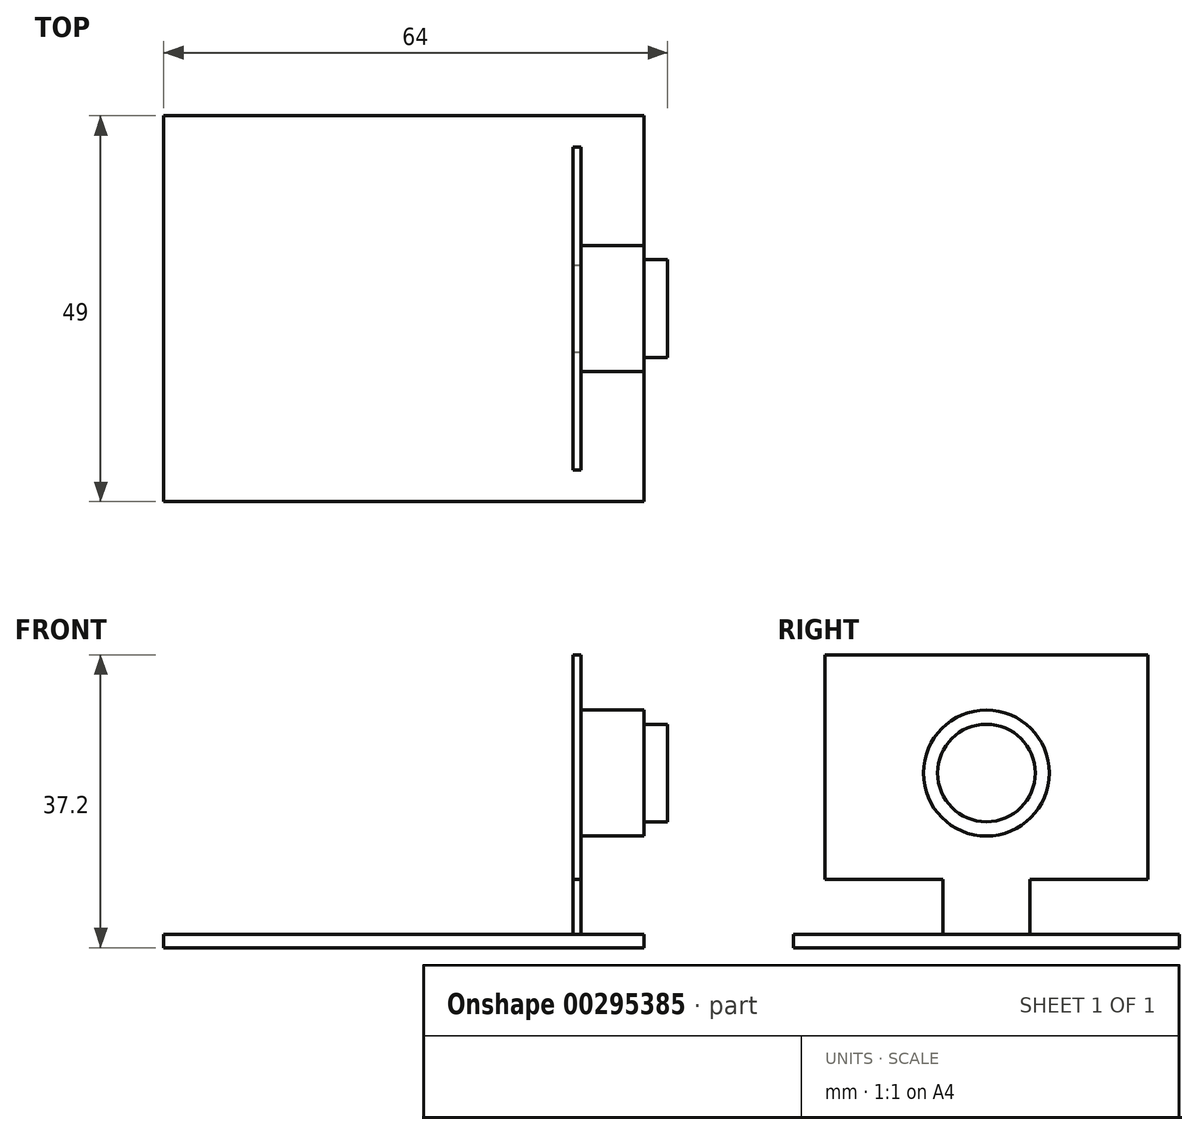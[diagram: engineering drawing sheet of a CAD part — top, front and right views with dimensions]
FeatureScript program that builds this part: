
annotation { "Feature Type Name" : "Feature", "Feature Type Description" : "" }
export const myFeature = defineFeature(function(context is Context, id is Id, definition is map)
    precondition{}
    {
        {
            var Q0;
            Q0=qCreatedBy(makeId("Top.planeOp"),FACE);
            var sketch = newSketch(context, id + "F0", { "sketchPlane" : qUnion([Q0])});
            skLineSegment(sketch, "E0.bottom", {"start": v(0, 0) * mm, "end": v(-61, 0) * mm});
            skLineSegment(sketch, "E0.top", {"start": v(0, 49) * mm, "end": v(-61, 49) * mm});
            skLineSegment(sketch, "E0.left", {"start": v(0, 0) * mm, "end": v(0, 49) * mm});
            skLineSegment(sketch, "E0.right", {"start": v(-61, 0) * mm, "end": v(-61, 49) * mm});
            skSolve(sketch);
        }
        {
            var Q0;
            Q0 = qSketchRegion(id + "F0", true);
            extrude(context, id + "F1", {"entities" : qUnion([Q0]), "depth" : 1.7 * mm});
        }
        {
            var Q0;
            Q0=qCreatedBy(makeId("Right.planeOp"),FACE);
            cPlane(context, id + "F2", {"entities" : qUnion([Q0]), "cplaneType" : CPlaneType.OFFSET, "offset" : 8 * mm, "oppositeDirection" : true, "width" : 150 * mm, "height" : 150 * mm});
        }
        {
            var Q0;
            Q0=qCreatedBy(id+"F2.planeOp",FACE);
            var sketch = newSketch(context, id + "F3", { "sketchPlane" : qUnion([Q0])});
            skLineSegment(sketch, "E1.bottom", {"start": v(19, 8.7) * mm, "end": v(30, 8.7) * mm});
            skLineSegment(sketch, "E1.top", {"start": v(19, 1.7) * mm, "end": v(30, 1.7) * mm});
            skLineSegment(sketch, "E1.left", {"start": v(19, 8.7) * mm, "end": v(19, 1.7) * mm});
            skLineSegment(sketch, "E1.right", {"start": v(30, 8.7) * mm, "end": v(30, 1.7) * mm});
            skLineSegment(sketch, "E2.bottom", {"start": v(45, 8.7) * mm, "end": v(4, 8.7) * mm});
            skLineSegment(sketch, "E2.top", {"start": v(45, 37.2) * mm, "end": v(4, 37.2) * mm});
            skLineSegment(sketch, "E2.left", {"start": v(45, 8.7) * mm, "end": v(45, 37.2) * mm});
            skLineSegment(sketch, "E2.right", {"start": v(4, 8.7) * mm, "end": v(4, 37.2) * mm});
            skSolve(sketch);
        }
        {
            var Q0;
            Q0 = qSketchRegion(id + "F3", true);
            extrude(context, id + "F4", {"entities" : qUnion([Q0]), "operationType" : NewBodyOperationType.ADD, "oppositeDirection" : true, "depth" : 1 * mm});
        }
        {
            var Q0;
            Q0=makeQuery(id+"F4.opExtrude","CAP_FACE",FACE,{"disambiguationData":[OSD([sQuery(id+"F3.wireOp",EDGE,"E1.top"),sQuery(id+"F3.wireOp",EDGE,"E1.left"),sQuery(id+"F3.wireOp",EDGE,"E1.right"),sQuery(id+"F3.wireOp",EDGE,"E2.bottom"),sQuery(id+"F3.wireOp",EDGE,"E2.top"),sQuery(id+"F3.wireOp",EDGE,"E2.left"),sQuery(id+"F3.wireOp",EDGE,"E2.right")])],"isStart":true});
            var sketch = newSketch(context, id + "F5", { "sketchPlane" : qUnion([Q0])});
            skCircle(sketch, "E3", {"center": v(24.5, 22.2) * mm, "radius": 8 * mm});
            skSolve(sketch);
        }
        {
            var Q0;
            Q0 = qSketchRegion(id + "F5", true);
            extrude(context, id + "F6", {"entities" : qUnion([Q0]), "operationType" : NewBodyOperationType.ADD, "depth" : 8 * mm});
        }
        {
            var Q0;
            Q0=makeQuery(id+"F6.opExtrude","CAP_FACE",FACE,{"disambiguationData":[OSD([sQuery(id+"F5.wireOp",EDGE,"E3")])],"isStart":false});
            var sketch = newSketch(context, id + "F7", { "sketchPlane" : qUnion([Q0])});
            skCircle(sketch, "E4", {"center": v(24.5, 22.2) * mm, "radius": 6.2 * mm});
            skSolve(sketch);
        }
        {
            var Q0;
            Q0 = qSketchRegion(id + "F7", true);
            extrude(context, id + "F8", {"entities" : qUnion([Q0]), "operationType" : NewBodyOperationType.ADD, "depth" : 3 * mm});
        }
    });
